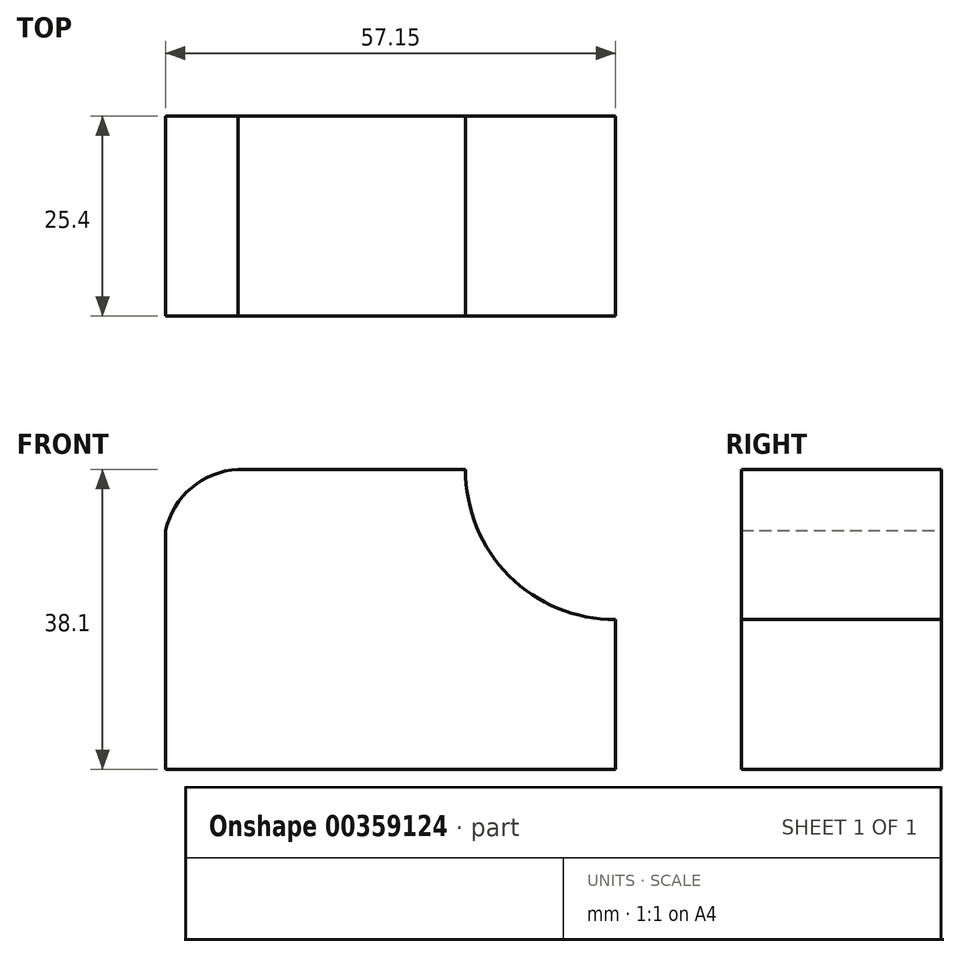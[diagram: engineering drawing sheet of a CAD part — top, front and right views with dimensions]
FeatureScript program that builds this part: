
annotation { "Feature Type Name" : "Feature", "Feature Type Description" : "" }
export const myFeature = defineFeature(function(context is Context, id is Id, definition is map)
    precondition{}
    {
        {
            var Q0;
            Q0=qCreatedBy(makeId("Front.planeOp"),FACE);
            var sketch = newSketch(context, id + "F0", { "sketchPlane" : qUnion([Q0])});
            skLineSegment(sketch, "E0", {"start": v(0, 0) * mm, "end": v(57.15, 0) * mm});
            skLineSegment(sketch, "E1", {"start": v(57.15, 0) * mm, "end": v(57.15, 38.1) * mm});
            skLineSegment(sketch, "E2", {"start": v(57.15, 38.1) * mm, "end": v(0, 38.1) * mm});
            skLineSegment(sketch, "E3", {"start": v(0, 38.1) * mm, "end": v(0, 0) * mm});
            skArc(sketch, "E4", {"start": v(10.16, 38.1) * mm, "mid": v(2.11, 34.6) * mm, "end": v(0, 26.08) * mm});
            skArc(sketch, "E5", {"start": v(38.1, 38.1) * mm, "mid": v(43.64, 24.6) * mm, "end": v(57.15, 19.05) * mm});
            skSolve(sketch);
        }
        {
            var Q0;
            {var subQ5=sQuery(id+"F0.wireOp",EDGE,"E0");Q0=makeQuery(id+"F0.imprint","IMPRINT",FACE,{"disambiguationData":[TD([[makeQuery(id+"F0.imprint","IMPRINT",EDGE,{"derivedFrom":subQ5}),1.0]])]});}
            extrude(context, id + "F1", {"entities" : qUnion([Q0]), "depth" : 25.4 * mm});
        }
    });
